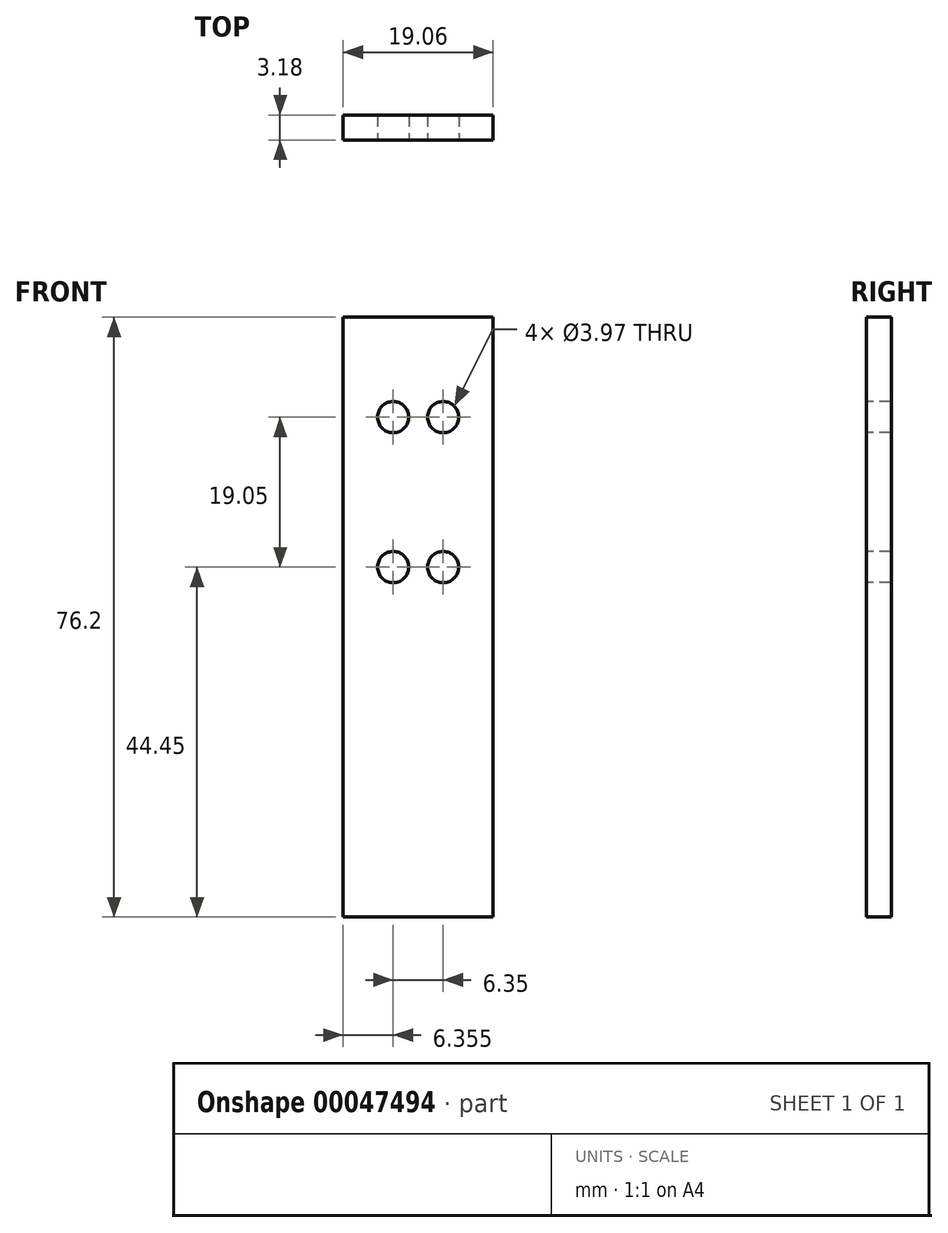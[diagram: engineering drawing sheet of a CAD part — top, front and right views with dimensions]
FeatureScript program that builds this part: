
annotation { "Feature Type Name" : "Feature", "Feature Type Description" : "" }
export const myFeature = defineFeature(function(context is Context, id is Id, definition is map)
    precondition{}
    {
        {
            var Q0;
            Q0=qCreatedBy(makeId("Top.planeOp"),FACE);
            var sketch = newSketch(context, id + "F0", { "sketchPlane" : qUnion([Q0])});
            skLineSegment(sketch, "E0.rect.bottom", {"start": v(9.53, 1.59) * mm, "end": v(-9.53, 1.59) * mm});
            skLineSegment(sketch, "E0.rect.top", {"start": v(9.53, -1.59) * mm, "end": v(-9.53, -1.59) * mm});
            skLineSegment(sketch, "E0.rect.left", {"start": v(9.53, 1.59) * mm, "end": v(9.53, -1.59) * mm});
            skLineSegment(sketch, "E0.rect.right", {"start": v(-9.53, 1.59) * mm, "end": v(-9.53, -1.59) * mm});
            skPoint(sketch, "E0.rect.middle", {"position": v(0, 0) * mm});
            skSolve(sketch);
        }
        {
            var Q0;
            Q0 = qSketchRegion(id + "F0", true);
            extrude(context, id + "F1", {"entities" : qUnion([Q0]), "depth" : 76.2 * mm, "symmetric" : true});
        }
        {
            var Q0;
            Q0=makeQuery(id+"F1.opExtrude","SWEPT_FACE",FACE,{"disambiguationData":[OSD([sQuery(id+"F0.wireOp",EDGE,"E0.rect.top")])]});
            var sketch = newSketch(context, id + "F2", { "sketchPlane" : qUnion([Q0])});
            skCircle(sketch, "E1", {"center": v(3.17, 25.4) * mm, "radius": 1.98 * mm});
            skCircle(sketch, "E2.MirrorC", {"center": v(-3.17, 25.4) * mm, "radius": 1.98 * mm});
            skCircle(sketch, "E3", {"center": v(3.18, 6.35) * mm, "radius": 1.98 * mm});
            skCircle(sketch, "E4.MirrorC", {"center": v(-3.18, 6.35) * mm, "radius": 1.98 * mm});
            skSolve(sketch);
        }
        {
            var Q0;
            Q0 = qSketchRegion(id + "F2", true);
            var Q1;
            Q1=makeQuery(id+"F1.opExtrude","SWEPT_BODY",BODY,{"disambiguationData":[OSD([sQuery(id+"F0.wireOp",EDGE,"E0.rect.bottom"),sQuery(id+"F0.wireOp",EDGE,"E0.rect.top"),sQuery(id+"F0.wireOp",EDGE,"E0.rect.left"),sQuery(id+"F0.wireOp",EDGE,"E0.rect.right")])]});
            extrude(context, id + "F3", {"entities" : qUnion([Q0]), "operationType" : NewBodyOperationType.REMOVE, "endBound" : BoundingType.UP_TO_BODY, "oppositeDirection" : true, "endBoundEntityBody" : qUnion([Q1]), "depth" : 25.4 * mm});
        }
    });
